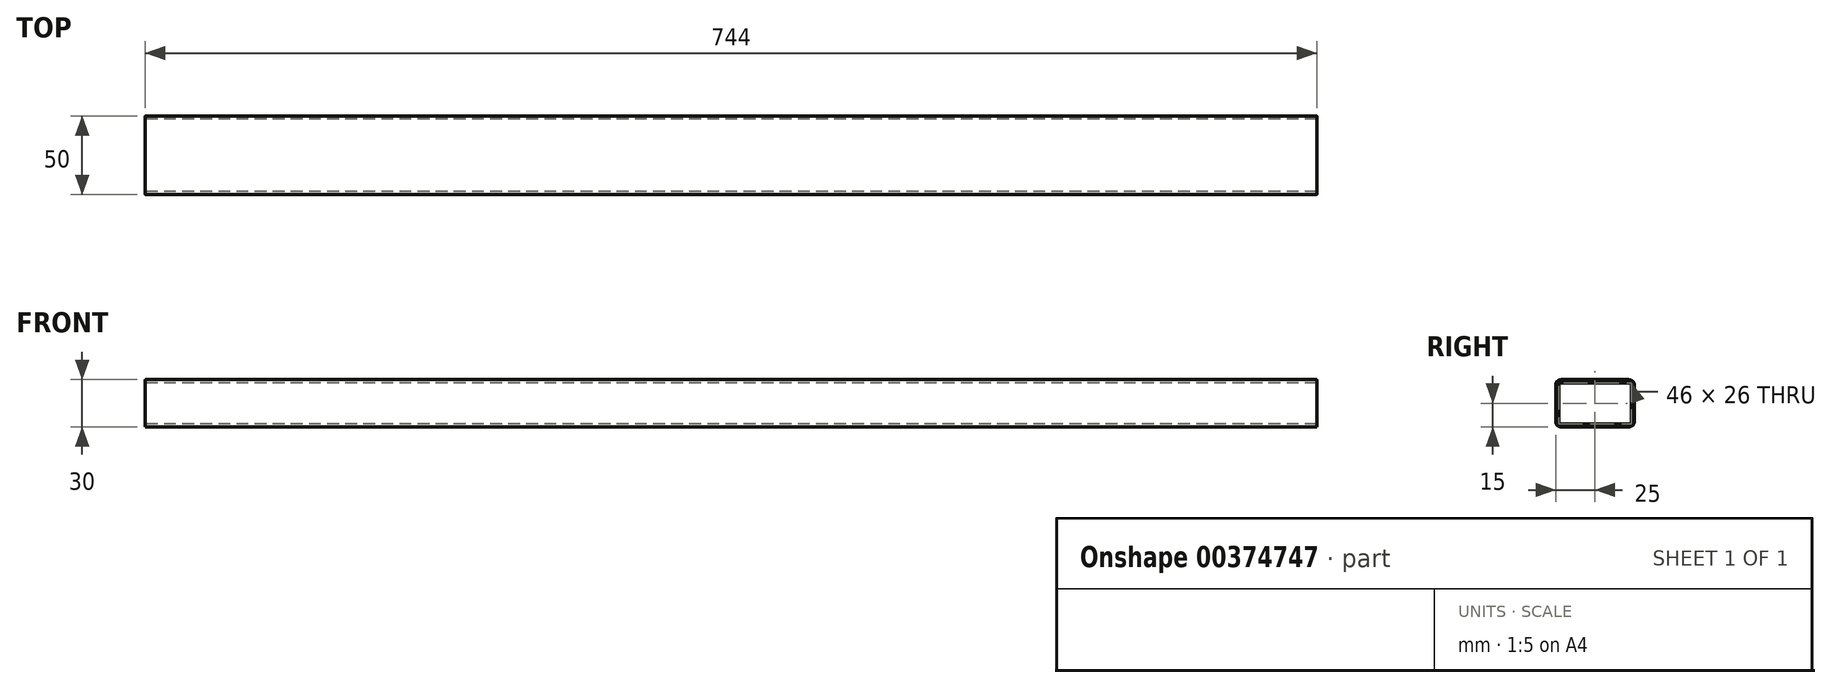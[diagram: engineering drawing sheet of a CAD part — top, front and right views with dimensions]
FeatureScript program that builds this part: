
annotation { "Feature Type Name" : "Feature", "Feature Type Description" : "" }
export const myFeature = defineFeature(function(context is Context, id is Id, definition is map)
    precondition{}
    {
        {
            var Q0;
            Q0=qCreatedBy(makeId("Right.planeOp"),FACE);
            var sketch = newSketch(context, id + "F0", { "sketchPlane" : qUnion([Q0])});
            skLineSegment(sketch, "E0.bottom", {"start": v(21.5, 15) * mm, "end": v(-21.5, 15) * mm});
            skLineSegment(sketch, "E0.top", {"start": v(21.5, -15) * mm, "end": v(-21.5, -15) * mm});
            skLineSegment(sketch, "E0.left", {"start": v(25, 11.5) * mm, "end": v(25, -11.5) * mm});
            skLineSegment(sketch, "E0.right", {"start": v(-25, 11.5) * mm, "end": v(-25, -11.5) * mm});
            skPoint(sketch, "E0.middle", {"position": v(0, 0) * mm});
            skLineSegment(sketch, "E1.bottom", {"start": v(23, 13) * mm, "end": v(-23, 13) * mm});
            skLineSegment(sketch, "E1.top", {"start": v(23, -13) * mm, "end": v(-23, -13) * mm});
            skLineSegment(sketch, "E1.left", {"start": v(23, 13) * mm, "end": v(23, -13) * mm});
            skLineSegment(sketch, "E1.right", {"start": v(-23, 13) * mm, "end": v(-23, -13) * mm});
            skPoint(sketch, "E2.visualSharp", {"position": v(-25, 15) * mm});
            skArc(sketch, "E2.filletArc", {"start": v(-21.5, 15) * mm, "mid": v(-23.97, 13.97) * mm, "end": v(-25, 11.5) * mm});
            skPoint(sketch, "E3.visualSharp", {"position": v(25, 15) * mm});
            skArc(sketch, "E3.filletArc", {"start": v(25, 11.5) * mm, "mid": v(23.97, 13.97) * mm, "end": v(21.5, 15) * mm});
            skPoint(sketch, "E4.visualSharp", {"position": v(25, -15) * mm});
            skArc(sketch, "E4.filletArc", {"start": v(21.5, -15) * mm, "mid": v(23.97, -13.97) * mm, "end": v(25, -11.5) * mm});
            skPoint(sketch, "E5.visualSharp", {"position": v(-25, -15) * mm});
            skArc(sketch, "E5.filletArc", {"start": v(-25, -11.5) * mm, "mid": v(-23.97, -13.97) * mm, "end": v(-21.5, -15) * mm});
            skSolve(sketch);
        }
        {
            var Q0;
            Q0=makeQuery(id+"F0.imprint","IMPRINT",FACE,{"disambiguationData":[TD([[makeQuery(id+"F0.imprint","IMPRINT",EDGE,{"derivedFrom":sQuery(id+"F0.wireOp",EDGE,"E0.bottom")}),1.0]])]});
            extrude(context, id + "F1", {"entities" : qUnion([Q0]), "depth" : 744 * mm, "offsetDistance" : 25 * mm});
        }
    });
